# Revit family: Atlas Geo Rimless WH Pan
name_source: partatom
category: Generic Models
units: mm (PartAtom-declared; Revit-internal decimal feet)

## family parameters
Always vertical = Yes
Can host rebar = No
Cut with Voids When Loaded = No
Host = Wall
Maintain Annotation Orientation = No
Part Type = Normal
Room Calculation Point = No
Round Connector Dimension = Use Diameter
Shared = No

## types (3) — shared parameters
Category = Wall Hung Pans
Ceramic = Ceramic
Colour = White
Manufacturer = Lecico SA
Material = Vitreous China
Plastic = Plastic
Technical Dimensions = W368 x H370 x D529mm
URL = https://www.lecicosa.co.za
zero-valued in all types: Default Elevation

## per-type parameters (varying)
| type | Product Code |
| Atlas Geo Rimless WH Pan no seat (Bolt holes 180) | GEOPANWHU0SLEUE |
| Atlas Geo Rimless Combo WH Pan MDF Seat (Bolt holes 180) | GEOBOXWHU0RIMDF |
| Atlas Geo Rimless Combo WH Pan 2004 Soft Close Seat (Bolt holes 180) | GEODUOWHU0SCSUE |

note: column(s) folded — value = type name in every type: Model

## geometry (parser evidence)
native form markers: Sweep x4
no freeform markers — native parametric forms only
